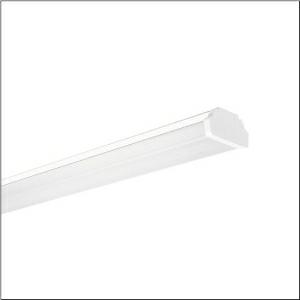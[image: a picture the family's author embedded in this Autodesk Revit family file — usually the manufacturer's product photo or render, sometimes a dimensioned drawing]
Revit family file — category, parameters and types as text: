
# Revit family: dus_r__31_gen_2_53bd811dv4a5c2_1568
name_source: partatom
category: Lighting Fixtures
units: mm (PartAtom-declared; Revit-internal decimal feet)

## family parameters
Cut with Voids When Loaded = No
Host = Face
Light Source = No
Part Type = Normal
Room Calculation Point = No
Round Connector Dimension = Use Diameter
Shared = No

## types (1)
- --- (1 x LED, 10860 lm, 61.4 W, 4000K)
    Apparent Load = 61 VA
    CIE Flux Codes = 50 78 94 90 100
    Color Rendering = 80
    Color Temperature = 4000K
    Default Elevation = 1800 mm
    Description = DUS® 31 Gen.2, luminaire insert, of sheet steel, coil coated, white, length: 1.535mm, width: 81mm, height: 90mm, 5x system unit, system units: 307mm, LED rated luminous flux: 10.860lm, light colour: 840, control gear: DALI 2, control gear: ECG DALI, with plug, 5-pole, with phase selection, mains connection: 220..240V, AC, 50/60Hz, rated input power: 61W, through-wiring accessed according to module size, primary optical cover: cover, of PMMA, light emission: direct distribution, primary light characteristic: symmetric, protection rating (complete): IP20, protection rating (LED compartment): IP50, insulation class (complete): insulation class I (protective earthing), certification: CE, ENEC, VDE, UKCA, impact resistance: IK03, permissible ambient temperature for indoor applications: -25..+35°C, corresponds to IFS (International Featured Standards) requirements for safety and quality in the food industry, reducing of maximum allowable ambient temperature of 5°C with ceiling mounting, packaging unit: 1 piece
    Height = 95 mm
    Lamp = 1 x LED
    Lamp Light Flux = 10860 lm
    Lamp Power = 61.4 W
    Lamp count = 1
    Length = 1535 mm
    Luminous efficacy = 177 lm/W
    Manufacturer = Siteco
    ModVariant = No
    Model = 53BD811DV4A5C2
    Mounting Place = Ceiling
    Mounting Type = Pendant
    Number of Poles = 1
    OnlyDefault = Yes
    Power Factor = 1
    Product Name = DUS® 31 Gen.2
    Product group = luminaire insert | ceiling pendant
    ProductGroupID = 902
    Protection Class = Protection class I
    Protection Degree = IP 20
    RLX_Detail_Level = 1
    RLX_Emergency_Light_Flux = 0 lm
    RLX_Emergency_Type = 0
    RLX_Emergency_Type_DB = No
    RlxData = <blob elided: 32201 chars, md5=080715cb>
    Socket = socket
    Standby Power = 0 W
    System Light Flux = 10860 lm
    System Power = 61 W
    Type Comments = factory setting: luminous flux: 100 % | dim-lin: 254 | 418 mA
    Type Image = l_1319596.jpg
    URL = http://relux.com
    VarID = @adj_063705
    Voltage = 0 V
    Weight = 0.00 kg
    Width = 81 mm

## geometry (parser evidence)
native form markers: Blend x4, Sweep x14
no freeform markers — native parametric forms only
